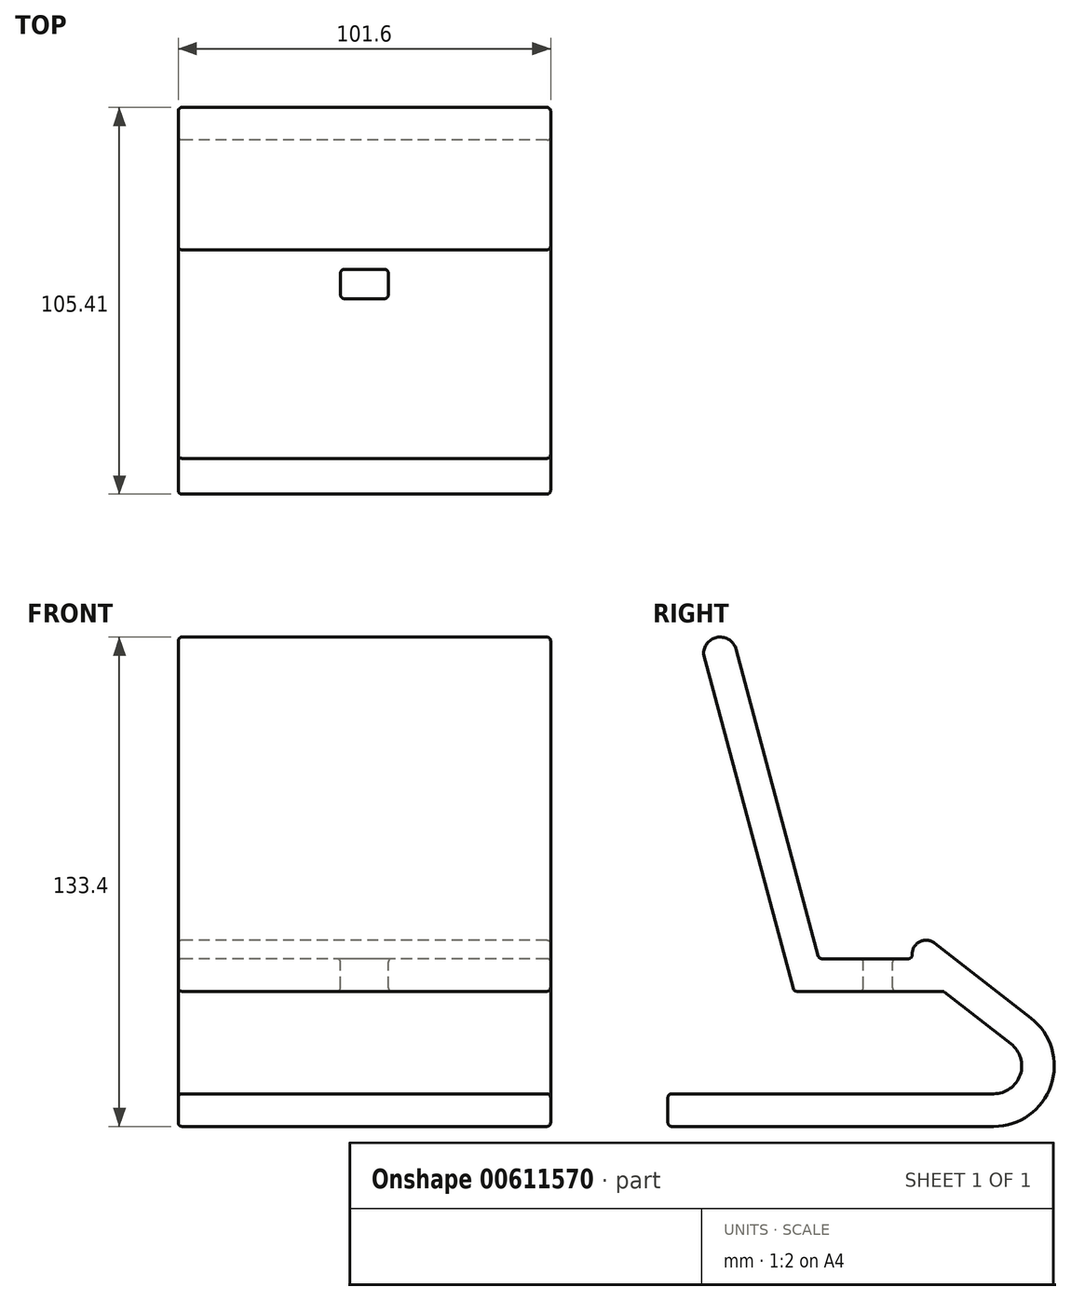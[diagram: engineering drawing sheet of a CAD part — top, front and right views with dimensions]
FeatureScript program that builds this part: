
annotation { "Feature Type Name" : "Feature", "Feature Type Description" : "" }
export const myFeature = defineFeature(function(context is Context, id is Id, definition is map)
    precondition{}
    {
        {
            var Q0;
            Q0=qCreatedBy(makeId("Right.planeOp"),FACE);
            var sketch = newSketch(context, id + "F0", { "sketchPlane" : qUnion([Q0])});
            skLineSegment(sketch, "E0", {"start": v(-57.27, -36.1) * mm, "end": v(31.63, -36.1) * mm});
            skArc(sketch, "E1", {"start": v(31.63, -36.1) * mm, "mid": v(38.83, -30.96) * mm, "end": v(36.3, -22.47) * mm});
            skLineSegment(sketch, "E2", {"start": v(-22.89, -8.17) * mm, "end": v(-47.54, 83.84) * mm});
            skArc(sketch, "E3.1", {"start": v(31.63, -45) * mm, "mid": v(47.24, -33.84) * mm, "end": v(41.75, -15.45) * mm});
            skLineSegment(sketch, "E4.0", {"start": v(-57.27, -45) * mm, "end": v(31.63, -45) * mm});
            skLineSegment(sketch, "E5", {"start": v(-16.07, 0.72) * mm, "end": v(9.33, 0.72) * mm});
            skLineSegment(sketch, "E6", {"start": v(-57.27, -36.1) * mm, "end": v(-57.27, -45) * mm});
            skLineSegment(sketch, "E7", {"start": v(-38.66, 85.05) * mm, "end": v(-16.07, 0.72) * mm});
            skPoint(sketch, "E8.visualSharp", {"position": v(9.33, 9.72) * mm});
            skLineSegment(sketch, "E9", {"start": v(36.3, -22.47) * mm, "end": v(17.88, -8.17) * mm});
            skLineSegment(sketch, "E10", {"start": v(17.88, -8.17) * mm, "end": v(-22.89, -8.17) * mm});
            skLineSegment(sketch, "E11", {"start": v(9.33, 0.72) * mm, "end": v(9.33, 1.94) * mm});
            skLineSegment(sketch, "E12", {"start": v(41.75, -15.45) * mm, "end": v(15.48, 4.95) * mm});
            skArc(sketch, "E13.filletArc", {"start": v(15.48, 4.95) * mm, "mid": v(11.47, 5.36) * mm, "end": v(9.33, 1.94) * mm});
            skArc(sketch, "E14", {"start": v(-38.66, 85.05) * mm, "mid": v(-43.63, 88.36) * mm, "end": v(-47.54, 83.84) * mm});
            skSolve(sketch);
        }
        {
            var Q0;
            Q0=makeQuery(id+"F0.imprint","IMPRINT",FACE,{"disambiguationData":[TD([[makeQuery(id+"F0.imprint","IMPRINT",EDGE,{"derivedFrom":sQuery(id+"F0.wireOp",EDGE,"E0")}),-1.0]])]});
            extrude(context, id + "F1", {"entities" : qUnion([Q0]), "endBound" : BoundingType.SYMMETRIC, "depth" : 101.6 * mm, "offsetDistance" : 25.4 * mm});
        }
        {
            var Q0;
            Q0=makeQuery(id+"F1.opExtrude","SWEPT_FACE",FACE,{"disambiguationData":[OSD([sQuery(id+"F0.wireOp",EDGE,"E5")])]});
            var sketch = newSketch(context, id + "F2", { "sketchPlane" : qUnion([Q0])});
            skLineSegment(sketch, "E15.bottom", {"start": v(6.5, -4) * mm, "end": v(-6.5, -4) * mm});
            skLineSegment(sketch, "E15.top", {"start": v(6.5, 4) * mm, "end": v(-6.5, 4) * mm});
            skLineSegment(sketch, "E15.left", {"start": v(6.5, -4) * mm, "end": v(6.5, 4) * mm});
            skLineSegment(sketch, "E15.right", {"start": v(-6.5, -4) * mm, "end": v(-6.5, 4) * mm});
            skPoint(sketch, "E15.middle", {"position": v(0, 0) * mm});
            skSolve(sketch);
        }
        {
            var Q0;
            Q0=makeQuery(id+"F2.imprint","IMPRINT",FACE,{"disambiguationData":[TD([[makeQuery(id+"F2.imprint","IMPRINT",EDGE,{"derivedFrom":sQuery(id+"F2.wireOp",EDGE,"E15.bottom")}),-1.0]])]});
            extrude(context, id + "F3", {"entities" : qUnion([Q0]), "operationType" : NewBodyOperationType.REMOVE, "oppositeDirection" : true, "depth" : 25.4 * mm, "offsetDistance" : 25.4 * mm});
        }
        {
            var Q0;
            Q0=makeQuery(id+"F1.opExtrude","SWEPT_FACE",FACE,{"disambiguationData":[OSD([sQuery(id+"F0.wireOp",EDGE,"E12")])]});
            var Q1;
            Q1=makeQuery(id+"F1.opExtrude","CAP_EDGE",EDGE,{"disambiguationData":[OSD([sQuery(id+"F0.wireOp",EDGE,"E12")])],"isStart":false});
            var Q2;
            Q2=makeQuery(id+"F1.opExtrude","CAP_EDGE",EDGE,{"disambiguationData":[OSD([sQuery(id+"F0.wireOp",EDGE,"E7")])],"isStart":false});
            var Q3;
            Q3=makeQuery(id+"F1.opExtrude","CAP_EDGE",EDGE,{"disambiguationData":[OSD([sQuery(id+"F0.wireOp",EDGE,"E2")])],"isStart":false});
            var Q4;
            Q4=makeQuery(id+"F1.opExtrude","SWEPT_EDGE",EDGE,{"disambiguationData":[OSD([sQuery(id+"F0.wireOp",EDGE,"E12"),sQuery(id+"F0.wireOp",EDGE,"E13.filletArc")])]});
            var Q5;
            Q5=makeQuery(id+"F1.opExtrude","SWEPT_FACE",FACE,{"disambiguationData":[OSD([sQuery(id+"F0.wireOp",EDGE,"E6")])]});
            var Q6;
            Q6=makeQuery(id+"F1.opExtrude","CAP_EDGE",EDGE,{"disambiguationData":[OSD([sQuery(id+"F0.wireOp",EDGE,"E1")])],"isStart":false});
            var Q7;
            Q7=makeQuery(id+"F1.opExtrude","CAP_EDGE",EDGE,{"disambiguationData":[OSD([sQuery(id+"F0.wireOp",EDGE,"E3.1")])],"isStart":true});
            var Q8;
            Q8=makeQuery(id+"F1.opExtrude","SWEPT_EDGE",EDGE,{"disambiguationData":[OSD([sQuery(id+"F0.wireOp",EDGE,"E3.1"),sQuery(id+"F0.wireOp",EDGE,"E12")])]});
            var Q9;
            Q9=makeQuery(id+"F1.opExtrude","SWEPT_FACE",FACE,{"disambiguationData":[OSD([sQuery(id+"F0.wireOp",EDGE,"E4.0")])]});
            var Q10;
            Q10=makeQuery(id+"F1.opExtrude","CAP_EDGE",EDGE,{"disambiguationData":[OSD([sQuery(id+"F0.wireOp",EDGE,"E14")])],"isStart":false});
            var Q11;
            Q11=makeQuery(id+"F1.opExtrude","SWEPT_FACE",FACE,{"disambiguationData":[OSD([sQuery(id+"F0.wireOp",EDGE,"E2")])]});
            var Q12;
            Q12=makeQuery(id+"F1.opExtrude","SWEPT_FACE",FACE,{"disambiguationData":[OSD([sQuery(id+"F0.wireOp",EDGE,"E3.1")])]});
            var Q13;
            Q13=makeQuery(id+"F1.opExtrude","CAP_EDGE",EDGE,{"disambiguationData":[OSD([sQuery(id+"F0.wireOp",EDGE,"E4.0")])],"isStart":false});
            var Q14;
            Q14=makeQuery(id+"F1.opExtrude","CAP_FACE",FACE,{"disambiguationData":[OSD([sQuery(id+"F0.wireOp",EDGE,"E0"),sQuery(id+"F0.wireOp",EDGE,"E1"),sQuery(id+"F0.wireOp",EDGE,"E2"),sQuery(id+"F0.wireOp",EDGE,"E3.1"),sQuery(id+"F0.wireOp",EDGE,"E4.0"),sQuery(id+"F0.wireOp",EDGE,"E5"),sQuery(id+"F0.wireOp",EDGE,"E6"),sQuery(id+"F0.wireOp",EDGE,"E7"),sQuery(id+"F0.wireOp",EDGE,"E9"),sQuery(id+"F0.wireOp",EDGE,"E10"),sQuery(id+"F0.wireOp",EDGE,"E11"),sQuery(id+"F0.wireOp",EDGE,"E12"),sQuery(id+"F0.wireOp",EDGE,"E13.filletArc"),sQuery(id+"F0.wireOp",EDGE,"E14")])],"isStart":false});
            var Q15;
            Q15=makeQuery(id+"F1.opExtrude","CAP_EDGE",EDGE,{"disambiguationData":[OSD([sQuery(id+"F0.wireOp",EDGE,"E3.1")])],"isStart":false});
            var Q16;
            Q16=makeQuery(id+"F1.opExtrude","CAP_EDGE",EDGE,{"disambiguationData":[OSD([sQuery(id+"F0.wireOp",EDGE,"E13.filletArc")])],"isStart":false});
            var Q17;
            Q17=makeQuery(id+"F1.opExtrude","SWEPT_FACE",FACE,{"disambiguationData":[OSD([sQuery(id+"F0.wireOp",EDGE,"E7")])]});
            var Q18;
            Q18=makeQuery(id+"F1.opExtrude","SWEPT_FACE",FACE,{"disambiguationData":[OSD([sQuery(id+"F0.wireOp",EDGE,"E1")])]});
            var Q19;
            Q19=makeQuery(id+"F1.opExtrude","SWEPT_FACE",FACE,{"disambiguationData":[OSD([sQuery(id+"F0.wireOp",EDGE,"E5")])]});
            var Q20;
            Q20=makeQuery(id+"F1.opExtrude","SWEPT_FACE",FACE,{"disambiguationData":[OSD([sQuery(id+"F0.wireOp",EDGE,"E0")])]});
            var Q21;
            Q21=makeQuery(id+"F1.opExtrude","CAP_FACE",FACE,{"disambiguationData":[OSD([sQuery(id+"F0.wireOp",EDGE,"E0"),sQuery(id+"F0.wireOp",EDGE,"E1"),sQuery(id+"F0.wireOp",EDGE,"E2"),sQuery(id+"F0.wireOp",EDGE,"E3.1"),sQuery(id+"F0.wireOp",EDGE,"E4.0"),sQuery(id+"F0.wireOp",EDGE,"E5"),sQuery(id+"F0.wireOp",EDGE,"E6"),sQuery(id+"F0.wireOp",EDGE,"E7"),sQuery(id+"F0.wireOp",EDGE,"E9"),sQuery(id+"F0.wireOp",EDGE,"E10"),sQuery(id+"F0.wireOp",EDGE,"E11"),sQuery(id+"F0.wireOp",EDGE,"E12"),sQuery(id+"F0.wireOp",EDGE,"E13.filletArc"),sQuery(id+"F0.wireOp",EDGE,"E14")])],"isStart":true});
            var Q22;
            Q22=makeQuery(id+"F1.opExtrude","SWEPT_FACE",FACE,{"disambiguationData":[OSD([sQuery(id+"F0.wireOp",EDGE,"E9")])]});
            var Q23;
            Q23=makeQuery(id+"F1.opExtrude","CAP_EDGE",EDGE,{"disambiguationData":[OSD([sQuery(id+"F0.wireOp",EDGE,"E5")])],"isStart":false});
            var Q24;
            Q24=makeQuery(id+"F1.opExtrude","SWEPT_FACE",FACE,{"disambiguationData":[OSD([sQuery(id+"F0.wireOp",EDGE,"E13.filletArc")])]});
            var Q25;
            Q25=makeQuery(id+"F1.opExtrude","CAP_EDGE",EDGE,{"disambiguationData":[OSD([sQuery(id+"F0.wireOp",EDGE,"E0")])],"isStart":false});
            var Q26;
            Q26=makeQuery(id+"F1.opExtrude","SWEPT_FACE",FACE,{"disambiguationData":[OSD([sQuery(id+"F0.wireOp",EDGE,"E14")])]});
            var Q27;
            Q27=makeQuery(id+"F1.opExtrude","SWEPT_EDGE",EDGE,{"disambiguationData":[OSD([sQuery(id+"F0.wireOp",EDGE,"E0"),sQuery(id+"F0.wireOp",EDGE,"E6")])]});
            var Q28;
            Q28=makeQuery(id+"F1.opExtrude","CAP_EDGE",EDGE,{"disambiguationData":[OSD([sQuery(id+"F0.wireOp",EDGE,"E7")])],"isStart":true});
            var Q29;
            Q29=makeQuery(id+"F1.opExtrude","CAP_EDGE",EDGE,{"disambiguationData":[OSD([sQuery(id+"F0.wireOp",EDGE,"E10")])],"isStart":false});
            var Q30;
            Q30=makeQuery(id+"F1.opExtrude","SWEPT_EDGE",EDGE,{"disambiguationData":[OSD([sQuery(id+"F0.wireOp",EDGE,"E5"),sQuery(id+"F0.wireOp",EDGE,"E7")])]});
            var Q31;
            Q31=makeQuery(id+"F1.opExtrude","CAP_EDGE",EDGE,{"disambiguationData":[OSD([sQuery(id+"F0.wireOp",EDGE,"E5")])],"isStart":true});
            var Q32;
            Q32=makeQuery(id+"F1.opExtrude","CAP_EDGE",EDGE,{"disambiguationData":[OSD([sQuery(id+"F0.wireOp",EDGE,"E14")])],"isStart":true});
            var Q33;
            Q33=makeQuery(id+"F1.opExtrude","SWEPT_EDGE",EDGE,{"disambiguationData":[OSD([sQuery(id+"F0.wireOp",EDGE,"E7"),sQuery(id+"F0.wireOp",EDGE,"E14")])]});
            var Q34;
            Q34=makeQuery(id+"F1.opExtrude","CAP_EDGE",EDGE,{"disambiguationData":[OSD([sQuery(id+"F0.wireOp",EDGE,"E13.filletArc")])],"isStart":true});
            var Q35;
            Q35=makeQuery(id+"F3.boolean.opBoolean","COPY",EDGE,{"derivedFrom":makeQuery(id+"F3.opExtrude","CAP_EDGE",EDGE,{"disambiguationData":[OSD([sQuery(id+"F2.wireOp",EDGE,"E15.right")])],"isStart":true})});
            var Q36;
            Q36=makeQuery(id+"F3.boolean.opBoolean","COPY",EDGE,{"derivedFrom":makeQuery(id+"F3.opExtrude","CAP_EDGE",EDGE,{"disambiguationData":[OSD([sQuery(id+"F2.wireOp",EDGE,"E15.left")])],"isStart":true})});
            var Q37;
            Q37=makeQuery(id+"F3.boolean.opBoolean","COPY",EDGE,{"derivedFrom":makeQuery(id+"F3.opExtrude","SWEPT_EDGE",EDGE,{"disambiguationData":[OSD([sQuery(id+"F2.wireOp",EDGE,"E15.top"),sQuery(id+"F2.wireOp",EDGE,"E15.left")])]})});
            var Q38;
            Q38=makeQuery(id+"F1.opExtrude","SWEPT_FACE",FACE,{"disambiguationData":[OSD([sQuery(id+"F0.wireOp",EDGE,"E11")])]});
            var Q39;
            Q39=makeQuery(id+"F1.opExtrude","CAP_EDGE",EDGE,{"disambiguationData":[OSD([sQuery(id+"F0.wireOp",EDGE,"E12")])],"isStart":true});
            var Q40;
            Q40=makeQuery(id+"F1.opExtrude","SWEPT_EDGE",EDGE,{"disambiguationData":[OSD([sQuery(id+"F0.wireOp",EDGE,"E4.0"),sQuery(id+"F0.wireOp",EDGE,"E6")])]});
            var Q41;
            Q41=makeQuery(id+"F1.opExtrude","SWEPT_EDGE",EDGE,{"disambiguationData":[OSD([sQuery(id+"F0.wireOp",EDGE,"E2"),sQuery(id+"F0.wireOp",EDGE,"E14")])]});
            var Q42;
            Q42=makeQuery(id+"F3.boolean.opBoolean","INTERSECT",EDGE,{"derivedFrom":[makeQuery(id+"F1.opExtrude","SWEPT_FACE",FACE,{"disambiguationData":[OSD([sQuery(id+"F0.wireOp",EDGE,"E10")])]}),makeQuery(id+"F3.opExtrude","SWEPT_FACE",FACE,{"disambiguationData":[OSD([sQuery(id+"F2.wireOp",EDGE,"E15.left")])]})]});
            var Q43;
            Q43=makeQuery(id+"F3.boolean.opBoolean","COPY",EDGE,{"derivedFrom":makeQuery(id+"F3.opExtrude","CAP_EDGE",EDGE,{"disambiguationData":[OSD([sQuery(id+"F2.wireOp",EDGE,"E15.bottom")])],"isStart":true})});
            var Q44;
            Q44=makeQuery(id+"F1.opExtrude","SWEPT_EDGE",EDGE,{"disambiguationData":[OSD([sQuery(id+"F0.wireOp",EDGE,"E11"),sQuery(id+"F0.wireOp",EDGE,"E13.filletArc")])]});
            var Q45;
            Q45=makeQuery(id+"F1.opExtrude","CAP_EDGE",EDGE,{"disambiguationData":[OSD([sQuery(id+"F0.wireOp",EDGE,"E1")])],"isStart":true});
            var Q46;
            Q46=makeQuery(id+"F1.opExtrude","CAP_EDGE",EDGE,{"disambiguationData":[OSD([sQuery(id+"F0.wireOp",EDGE,"E2")])],"isStart":true});
            var Q47;
            Q47=makeQuery(id+"F1.opExtrude","SWEPT_EDGE",EDGE,{"disambiguationData":[OSD([sQuery(id+"F0.wireOp",EDGE,"E9"),sQuery(id+"F0.wireOp",EDGE,"E10")])]});
            var Q48;
            Q48=makeQuery(id+"F1.opExtrude","SWEPT_FACE",FACE,{"disambiguationData":[OSD([sQuery(id+"F0.wireOp",EDGE,"E10")])]});
            var Q49;
            Q49=makeQuery(id+"F3.boolean.opBoolean","COPY",FACE,{"derivedFrom":makeQuery(id+"F3.opExtrude","SWEPT_FACE",FACE,{"disambiguationData":[OSD([sQuery(id+"F2.wireOp",EDGE,"E15.left")])]})});
            var Q50;
            Q50=makeQuery(id+"F1.opExtrude","SWEPT_EDGE",EDGE,{"disambiguationData":[OSD([sQuery(id+"F0.wireOp",EDGE,"E0"),sQuery(id+"F0.wireOp",EDGE,"E1")])]});
            var Q51;
            Q51=makeQuery(id+"F3.boolean.opBoolean","COPY",EDGE,{"derivedFrom":makeQuery(id+"F3.opExtrude","SWEPT_EDGE",EDGE,{"disambiguationData":[OSD([sQuery(id+"F2.wireOp",EDGE,"E15.top"),sQuery(id+"F2.wireOp",EDGE,"E15.right")])]})});
            var Q52;
            Q52=makeQuery(id+"F3.boolean.opBoolean","COPY",FACE,{"derivedFrom":makeQuery(id+"F3.opExtrude","SWEPT_FACE",FACE,{"disambiguationData":[OSD([sQuery(id+"F2.wireOp",EDGE,"E15.bottom")])]})});
            var Q53;
            Q53=makeQuery(id+"F1.opExtrude","CAP_EDGE",EDGE,{"disambiguationData":[OSD([sQuery(id+"F0.wireOp",EDGE,"E9")])],"isStart":true});
            var Q54;
            Q54=makeQuery(id+"F1.opExtrude","SWEPT_EDGE",EDGE,{"disambiguationData":[OSD([sQuery(id+"F0.wireOp",EDGE,"E2"),sQuery(id+"F0.wireOp",EDGE,"E10")])]});
            var Q55;
            Q55=makeQuery(id+"F1.opExtrude","CAP_EDGE",EDGE,{"disambiguationData":[OSD([sQuery(id+"F0.wireOp",EDGE,"E4.0")])],"isStart":true});
            var Q56;
            Q56=makeQuery(id+"F1.opExtrude","CAP_EDGE",EDGE,{"disambiguationData":[OSD([sQuery(id+"F0.wireOp",EDGE,"E9")])],"isStart":false});
            var Q57;
            Q57=makeQuery(id+"F1.opExtrude","CAP_EDGE",EDGE,{"disambiguationData":[OSD([sQuery(id+"F0.wireOp",EDGE,"E6")])],"isStart":false});
            var Q58;
            Q58=makeQuery(id+"F1.opExtrude","SWEPT_EDGE",EDGE,{"disambiguationData":[OSD([sQuery(id+"F0.wireOp",EDGE,"E1"),sQuery(id+"F0.wireOp",EDGE,"E9")])]});
            var Q59;
            Q59=makeQuery(id+"F1.opExtrude","CAP_EDGE",EDGE,{"disambiguationData":[OSD([sQuery(id+"F0.wireOp",EDGE,"E10")])],"isStart":true});
            var Q60;
            Q60=makeQuery(id+"F1.opExtrude","CAP_EDGE",EDGE,{"disambiguationData":[OSD([sQuery(id+"F0.wireOp",EDGE,"E0")])],"isStart":true});
            var Q61;
            Q61=makeQuery(id+"F3.boolean.opBoolean","COPY",FACE,{"derivedFrom":makeQuery(id+"F3.opExtrude","SWEPT_FACE",FACE,{"disambiguationData":[OSD([sQuery(id+"F2.wireOp",EDGE,"E15.top")])]})});
            var Q62;
            Q62=makeQuery(id+"F3.boolean.opBoolean","COPY",FACE,{"derivedFrom":makeQuery(id+"F3.opExtrude","SWEPT_FACE",FACE,{"disambiguationData":[OSD([sQuery(id+"F2.wireOp",EDGE,"E15.right")])]})});
            var Q63;
            Q63=makeQuery(id+"F1.opExtrude","SWEPT_EDGE",EDGE,{"disambiguationData":[OSD([sQuery(id+"F0.wireOp",EDGE,"E3.1"),sQuery(id+"F0.wireOp",EDGE,"E4.0")])]});
            var Q64;
            Q64=makeQuery(id+"F1.opExtrude","CAP_EDGE",EDGE,{"disambiguationData":[OSD([sQuery(id+"F0.wireOp",EDGE,"E11")])],"isStart":false});
            var Q65;
            Q65=makeQuery(id+"F1.opExtrude","SWEPT_EDGE",EDGE,{"disambiguationData":[OSD([sQuery(id+"F0.wireOp",EDGE,"E5"),sQuery(id+"F0.wireOp",EDGE,"E11")])]});
            var Q66;
            Q66=makeQuery(id+"F1.opExtrude","CAP_EDGE",EDGE,{"disambiguationData":[OSD([sQuery(id+"F0.wireOp",EDGE,"E6")])],"isStart":true});
            var Q67;
            Q67=makeQuery(id+"F3.boolean.opBoolean","INTERSECT",EDGE,{"derivedFrom":[makeQuery(id+"F1.opExtrude","SWEPT_FACE",FACE,{"disambiguationData":[OSD([sQuery(id+"F0.wireOp",EDGE,"E10")])]}),makeQuery(id+"F3.opExtrude","SWEPT_FACE",FACE,{"disambiguationData":[OSD([sQuery(id+"F2.wireOp",EDGE,"E15.top")])]})]});
            var Q68;
            Q68=makeQuery(id+"F3.boolean.opBoolean","COPY",EDGE,{"derivedFrom":makeQuery(id+"F3.opExtrude","CAP_EDGE",EDGE,{"disambiguationData":[OSD([sQuery(id+"F2.wireOp",EDGE,"E15.top")])],"isStart":true})});
            var Q69;
            Q69=makeQuery(id+"F3.boolean.opBoolean","INTERSECT",EDGE,{"derivedFrom":[makeQuery(id+"F1.opExtrude","SWEPT_FACE",FACE,{"disambiguationData":[OSD([sQuery(id+"F0.wireOp",EDGE,"E10")])]}),makeQuery(id+"F3.opExtrude","SWEPT_FACE",FACE,{"disambiguationData":[OSD([sQuery(id+"F2.wireOp",EDGE,"E15.right")])]})]});
            var Q70;
            Q70=makeQuery(id+"F1.opExtrude","CAP_EDGE",EDGE,{"disambiguationData":[OSD([sQuery(id+"F0.wireOp",EDGE,"E11")])],"isStart":true});
            var Q71;
            Q71=makeQuery(id+"F3.boolean.opBoolean","COPY",EDGE,{"derivedFrom":makeQuery(id+"F3.opExtrude","SWEPT_EDGE",EDGE,{"disambiguationData":[OSD([sQuery(id+"F2.wireOp",EDGE,"E15.bottom"),sQuery(id+"F2.wireOp",EDGE,"E15.right")])]})});
            var Q72;
            Q72=makeQuery(id+"F3.boolean.opBoolean","INTERSECT",EDGE,{"derivedFrom":[makeQuery(id+"F1.opExtrude","SWEPT_FACE",FACE,{"disambiguationData":[OSD([sQuery(id+"F0.wireOp",EDGE,"E10")])]}),makeQuery(id+"F3.opExtrude","SWEPT_FACE",FACE,{"disambiguationData":[OSD([sQuery(id+"F2.wireOp",EDGE,"E15.bottom")])]})]});
            var Q73;
            Q73=makeQuery(id+"F3.boolean.opBoolean","COPY",EDGE,{"derivedFrom":makeQuery(id+"F3.opExtrude","SWEPT_EDGE",EDGE,{"disambiguationData":[OSD([sQuery(id+"F2.wireOp",EDGE,"E15.bottom"),sQuery(id+"F2.wireOp",EDGE,"E15.left")])]})});
            fillet(context, id + "F4", {"entities" : qUnion([Q0, Q1, Q2, Q3, Q4, Q5, Q6, Q7, Q8, Q9, Q10, Q11, Q12, Q13, Q14, Q15, Q16, Q17, Q18, Q19, Q20, Q21, Q22, Q23, Q24, Q25, Q26, Q27, Q28, Q29, Q30, Q31, Q32, Q33, Q34, Q35, Q36, Q37, Q38, Q39, Q40, Q41, Q42, Q43, Q44, Q45, Q46, Q47, Q48, Q49, Q50, Q51, Q52, Q53, Q54, Q55, Q56, Q57, Q58, Q59, Q60, Q61, Q62, Q63, Q64, Q65, Q66, Q67, Q68, Q69, Q70, Q71, Q72, Q73]), "radius" : 1 * mm, "tangentPropagation" : true, "allowEdgeOverflow" : false});
        }
    });
